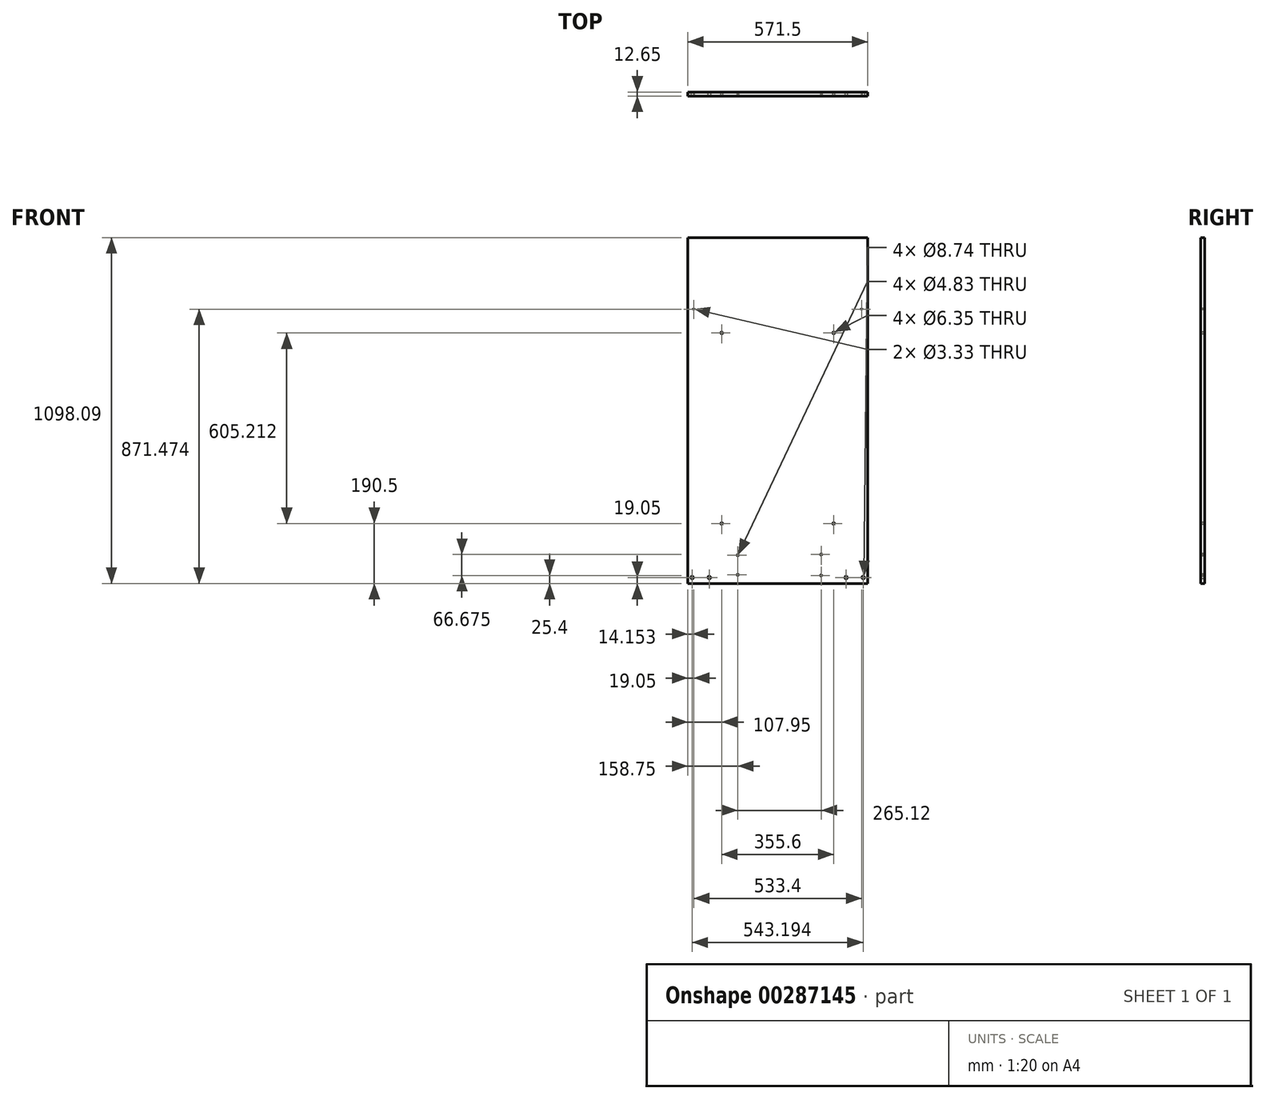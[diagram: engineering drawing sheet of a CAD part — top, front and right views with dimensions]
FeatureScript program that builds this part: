
annotation { "Feature Type Name" : "Feature", "Feature Type Description" : "" }
export const myFeature = defineFeature(function(context is Context, id is Id, definition is map)
    precondition{}
    {
        {
            var Q0;
            Q0=qCreatedBy(makeId("Front.planeOp"),FACE);
            var sketch = newSketch(context, id + "F0", { "sketchPlane" : qUnion([Q0])});
            skLineSegment(sketch, "E0.bottom", {"start": v(0, 0) * mm, "end": v(571.5, 0) * mm});
            skLineSegment(sketch, "E0.top", {"start": v(0, 1098.1) * mm, "end": v(571.5, 1098.1) * mm});
            skLineSegment(sketch, "E0.left", {"start": v(0, 0) * mm, "end": v(0, 1098.1) * mm});
            skLineSegment(sketch, "E0.right", {"start": v(571.5, 0) * mm, "end": v(571.5, 1098.1) * mm});
            skSolve(sketch);
        }
        {
            var Q0;
            Q0=makeQuery(id+"F0.imprint","IMPRINT",FACE,{"disambiguationData":[TD([[makeQuery(id+"F0.imprint","IMPRINT",EDGE,{"derivedFrom":sQuery(id+"F0.wireOp",EDGE,"E0.bottom")}),1.0]])]});
            extrude(context, id + "F1", {"entities" : qUnion([Q0]), "depth" : 12.65 * mm});
        }
        {
            var Q0;
            Q0=makeQuery(id+"F1.opExtrude","CAP_FACE",FACE,{"disambiguationData":[OSD([sQuery(id+"F0.wireOp",EDGE,"E0.bottom"),sQuery(id+"F0.wireOp",EDGE,"E0.top"),sQuery(id+"F0.wireOp",EDGE,"E0.left"),sQuery(id+"F0.wireOp",EDGE,"E0.right")])],"isStart":false});
            var sketch = newSketch(context, id + "F2", { "sketchPlane" : qUnion([Q0])});
            skCircle(sketch, "E1", {"center": v(14.15, 19.05) * mm, "radius": 4.37 * mm});
            skCircle(sketch, "E2", {"center": v(68.4, 19.05) * mm, "radius": 4.37 * mm});
            skCircle(sketch, "E3.MirrorC", {"center": v(503.1, 19.05) * mm, "radius": 4.37 * mm});
            skCircle(sketch, "E4.MirrorC", {"center": v(557.35, 19.05) * mm, "radius": 4.37 * mm});
            skCircle(sketch, "E5", {"center": v(107.95, 190.5) * mm, "radius": 3.18 * mm});
            skCircle(sketch, "E6", {"center": v(463.55, 190.5) * mm, "radius": 3.18 * mm});
            skLineSegment(sketch, "E7", {"start": v(285.75, 25.4) * mm, "end": v(423.87, 25.4) * mm});
            skCircle(sketch, "E8", {"center": v(423.87, 25.4) * mm, "radius": 2.41 * mm});
            skLineSegment(sketch, "E9.0", {"start": v(285.75, 92.08) * mm, "end": v(423.87, 92.08) * mm});
            skCircle(sketch, "E10", {"center": v(423.87, 92.08) * mm, "radius": 2.41 * mm});
            skLineSegment(sketch, "E11", {"start": v(423.87, 25.4) * mm, "end": v(423.87, 92.08) * mm});
            skLineSegment(sketch, "E12", {"start": v(423.87, 58.74) * mm, "end": v(275.86, 58.74) * mm});
            skLineSegment(sketch, "E13", {"start": v(158.75, 58.74) * mm, "end": v(158.75, 27.62) * mm});
            skLineSegment(sketch, "E14.MirrorCS", {"start": v(158.75, 58.74) * mm, "end": v(158.75, 89.85) * mm});
            skCircle(sketch, "E15", {"center": v(158.75, 89.85) * mm, "radius": 2.41 * mm});
            skCircle(sketch, "E16", {"center": v(158.75, 27.62) * mm, "radius": 2.41 * mm});
            skCircle(sketch, "E17", {"center": v(107.95, 795.71) * mm, "radius": 3.18 * mm});
            skCircle(sketch, "E18", {"center": v(463.55, 795.71) * mm, "radius": 3.18 * mm});
            skLineSegment(sketch, "E19", {"start": v(0, 1098.1) * mm, "end": v(0, 871.47) * mm});
            skLineSegment(sketch, "E20", {"start": v(285.75, 1098.1) * mm, "end": v(285.75, 912.8) * mm});
            skPoint(sketch, "E20.endSnap0", {"position": v(285.75, 1098.1) * mm});
            skLineSegment(sketch, "E21", {"start": v(0, 1098.1) * mm, "end": v(571.5, 1098.1) * mm});
            skLineSegment(sketch, "E22.0", {"start": v(19.05, 1098.1) * mm, "end": v(19.05, 871.47) * mm});
            skCircle(sketch, "E23", {"center": v(19.05, 871.47) * mm, "radius": 1.66 * mm});
            skCircle(sketch, "E24.MirrorC", {"center": v(552.45, 871.47) * mm, "radius": 1.66 * mm});
            skLineSegment(sketch, "E25", {"start": v(0, 0) * mm, "end": v(571.5, 0) * mm});
            skLineSegment(sketch, "E26", {"start": v(107.95, 190.5) * mm, "end": v(107.95, 0) * mm});
            skLineSegment(sketch, "E27", {"start": v(0, 0) * mm, "end": v(107.95, 0) * mm});
            skLineSegment(sketch, "E28", {"start": v(14.15, 19.05) * mm, "end": v(14.15, 0) * mm});
            skLineSegment(sketch, "E29", {"start": v(68.4, 19.05) * mm, "end": v(68.4, 0) * mm});
            skLineSegment(sketch, "E30", {"start": v(423.87, 92.08) * mm, "end": v(423.87, 0) * mm});
            skLineSegment(sketch, "E31", {"start": v(571.5, 0) * mm, "end": v(423.87, 0) * mm});
            skLineSegment(sketch, "E32", {"start": v(14.15, 0) * mm, "end": v(0, 0) * mm});
            skLineSegment(sketch, "E33", {"start": v(158.75, 89.85) * mm, "end": v(158.75, 0) * mm});
            skLineSegment(sketch, "E34", {"start": v(107.95, 795.71) * mm, "end": v(107.95, 1098.1) * mm});
            skLineSegment(sketch, "E35", {"start": v(571.5, 1098.1) * mm, "end": v(571.5, 0) * mm});
            skSolve(sketch);
        }
        {
            var Q0;
            Q0 = qSketchRegion(id + "F2", true);
            extrude(context, id + "F3", {"entities" : qUnion([Q0]), "operationType" : NewBodyOperationType.REMOVE, "oppositeDirection" : true, "depth" : 12.65 * mm});
        }
    });
